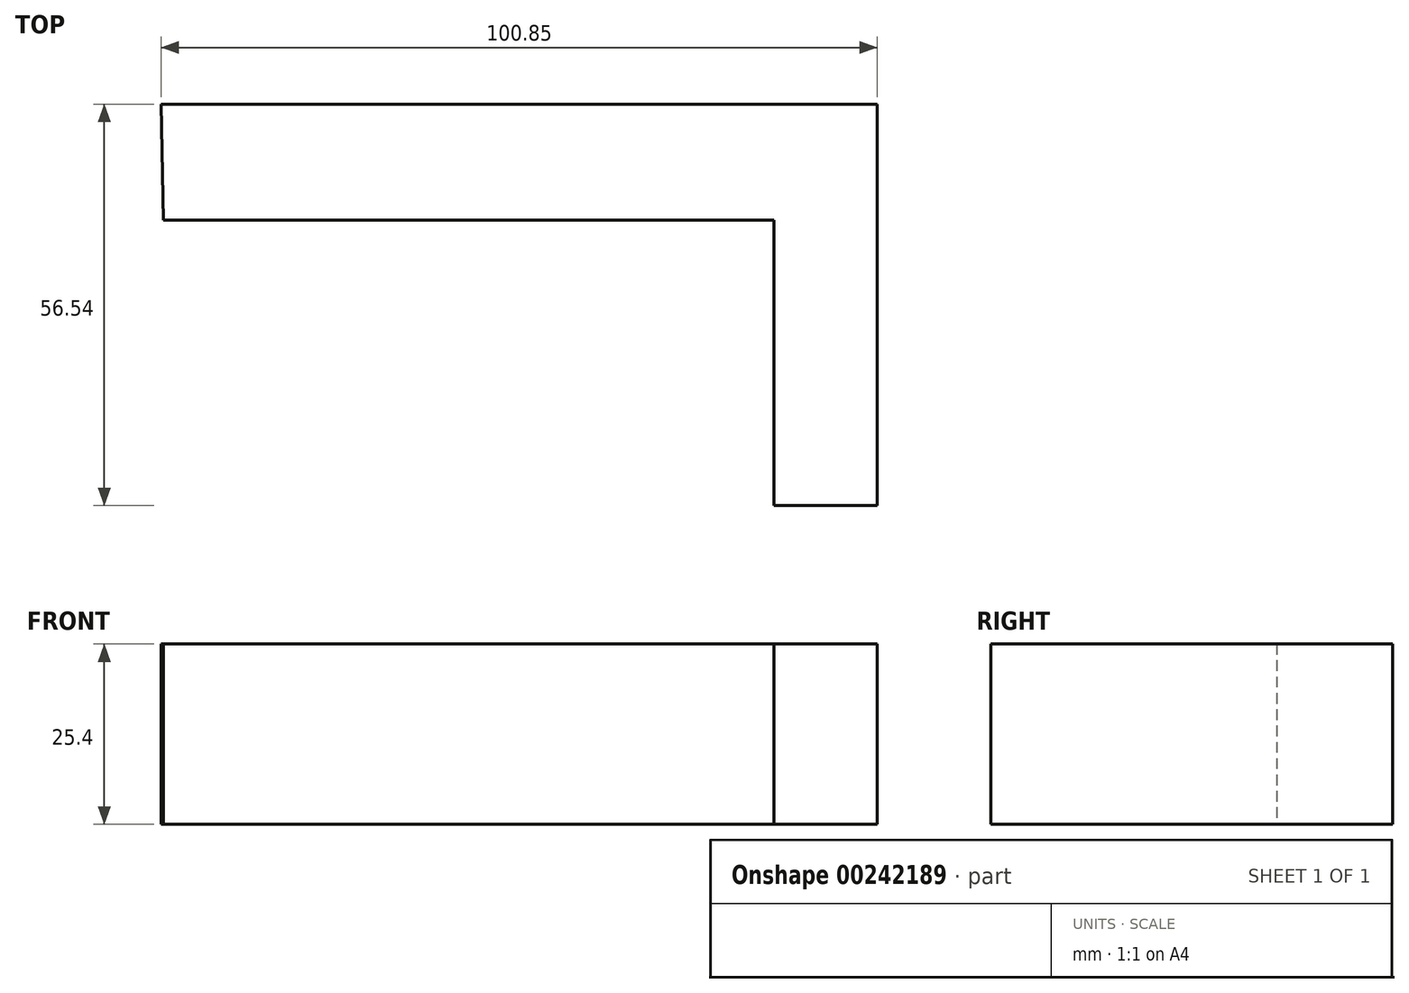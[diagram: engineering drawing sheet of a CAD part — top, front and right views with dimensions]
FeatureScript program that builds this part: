
annotation { "Feature Type Name" : "Feature", "Feature Type Description" : "" }
export const myFeature = defineFeature(function(context is Context, id is Id, definition is map)
    precondition{}
    {
        {
            var Q0;
            Q0=qCreatedBy(makeId("Top.planeOp"),FACE);
            var sketch = newSketch(context, id + "F0", { "sketchPlane" : qUnion([Q0])});
            skLineSegment(sketch, "E0", {"start": v(-39.93, 41.24) * mm, "end": v(60.92, 41.24) * mm});
            skLineSegment(sketch, "E1", {"start": v(60.92, 41.24) * mm, "end": v(60.92, -15.3) * mm});
            skLineSegment(sketch, "E2", {"start": v(60.92, -15.3) * mm, "end": v(46.34, -15.3) * mm});
            skLineSegment(sketch, "E3", {"start": v(46.34, -15.3) * mm, "end": v(46.34, 24.92) * mm});
            skLineSegment(sketch, "E4", {"start": v(46.34, 24.92) * mm, "end": v(-39.64, 24.92) * mm});
            skLineSegment(sketch, "E5", {"start": v(-39.64, 24.92) * mm, "end": v(-39.93, 41.24) * mm});
            skSolve(sketch);
        }
        {
            var Q0;
            Q0 = qSketchRegion(id + "F0", true);
            extrude(context, id + "F1", {"entities" : qUnion([Q0]), "depth" : 25.4 * mm});
        }
    });
